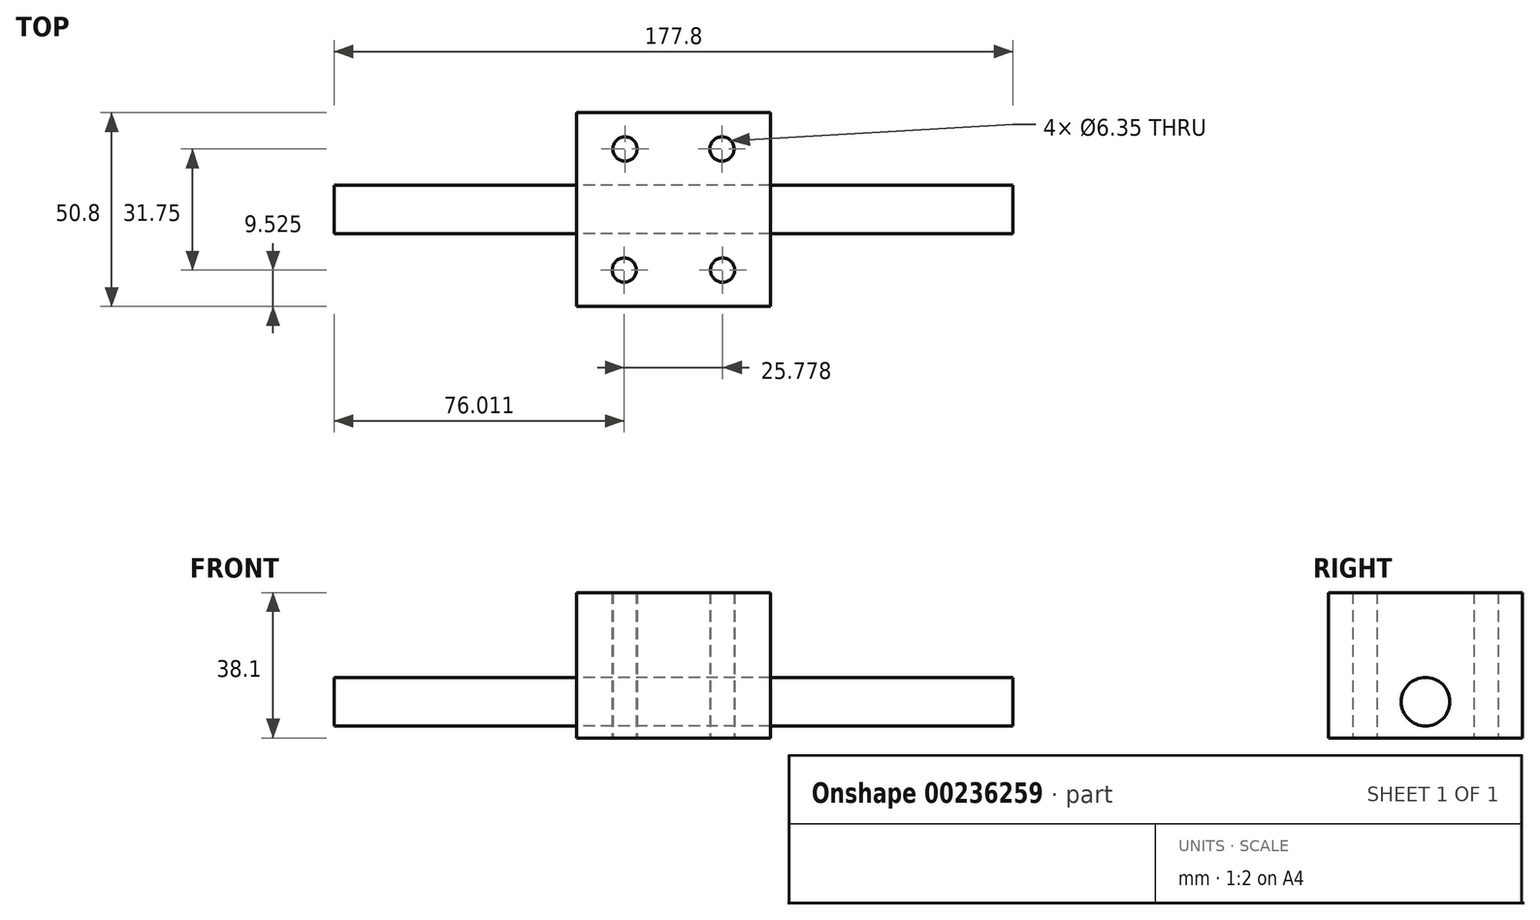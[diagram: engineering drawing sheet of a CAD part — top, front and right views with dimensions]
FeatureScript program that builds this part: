
annotation { "Feature Type Name" : "Feature", "Feature Type Description" : "" }
export const myFeature = defineFeature(function(context is Context, id is Id, definition is map)
    precondition{}
    {
        {
            var Q0;
            Q0=qCreatedBy(makeId("Top.planeOp"),FACE);
            var sketch = newSketch(context, id + "F0", { "sketchPlane" : qUnion([Q0])});
            skLineSegment(sketch, "E0.bottom", {"start": v(25.4, 25.4) * mm, "end": v(-25.4, 25.4) * mm});
            skLineSegment(sketch, "E0.top", {"start": v(25.4, -25.4) * mm, "end": v(-25.4, -25.4) * mm});
            skLineSegment(sketch, "E0.left", {"start": v(25.4, 25.4) * mm, "end": v(25.4, -25.4) * mm});
            skLineSegment(sketch, "E0.right", {"start": v(-25.4, 25.4) * mm, "end": v(-25.4, -25.4) * mm});
            skPoint(sketch, "E0.middle", {"position": v(0, 0) * mm});
            skCircle(sketch, "E1", {"center": v(-12.7, 15.88) * mm, "radius": 3.18 * mm});
            skCircle(sketch, "E2.MirrorC", {"center": v(12.7, 15.88) * mm, "radius": 3.18 * mm});
            skCircle(sketch, "E3", {"center": v(-12.89, -15.88) * mm, "radius": 3.18 * mm});
            skCircle(sketch, "E4.MirrorC", {"center": v(12.89, -15.88) * mm, "radius": 3.18 * mm});
            skSolve(sketch);
        }
        {
            var Q0;
            Q0 = qSketchRegion(id + "F0", true);
            extrude(context, id + "F1", {"entities" : qUnion([Q0]), "endBound" : BoundingType.SYMMETRIC, "depth" : 38.1 * mm});
        }
        {
            var Q0;
            Q0=makeQuery(id+"F1.opExtrude","SWEPT_BODY",BODY,{"disambiguationData":[OSD([sQuery(id+"F0.wireOp",EDGE,"E0.bottom"),sQuery(id+"F0.wireOp",EDGE,"E0.top"),sQuery(id+"F0.wireOp",EDGE,"E0.left"),sQuery(id+"F0.wireOp",EDGE,"E0.right"),sQuery(id+"F0.wireOp",EDGE,"E1"),sQuery(id+"F0.wireOp",EDGE,"E2.MirrorC"),sQuery(id+"F0.wireOp",EDGE,"E3"),sQuery(id+"F0.wireOp",EDGE,"E4.MirrorC")])]});
            var Q1;
            Q1=qCreatedBy(makeId("Right.planeOp"),FACE);
            mirror(context, id + "F2", {"operationType" : NewBodyOperationType.ADD, "entities" : qUnion([Q0]), "mirrorPlane" : qUnion([Q1])});
        }
        {
            var Q0;
            Q0=qCreatedBy(makeId("Right.planeOp"),FACE);
            var sketch = newSketch(context, id + "F3", { "sketchPlane" : qUnion([Q0])});
            skCircle(sketch, "E5", {"center": v(0, -9.53) * mm, "radius": 6.35 * mm});
            skSolve(sketch);
        }
        {
            var Q0;
            Q0 = qSketchRegion(id + "F3", true);
            extrude(context, id + "F4", {"entities" : qUnion([Q0]), "endBound" : BoundingType.SYMMETRIC, "depth" : 177.8 * mm});
        }
    });
